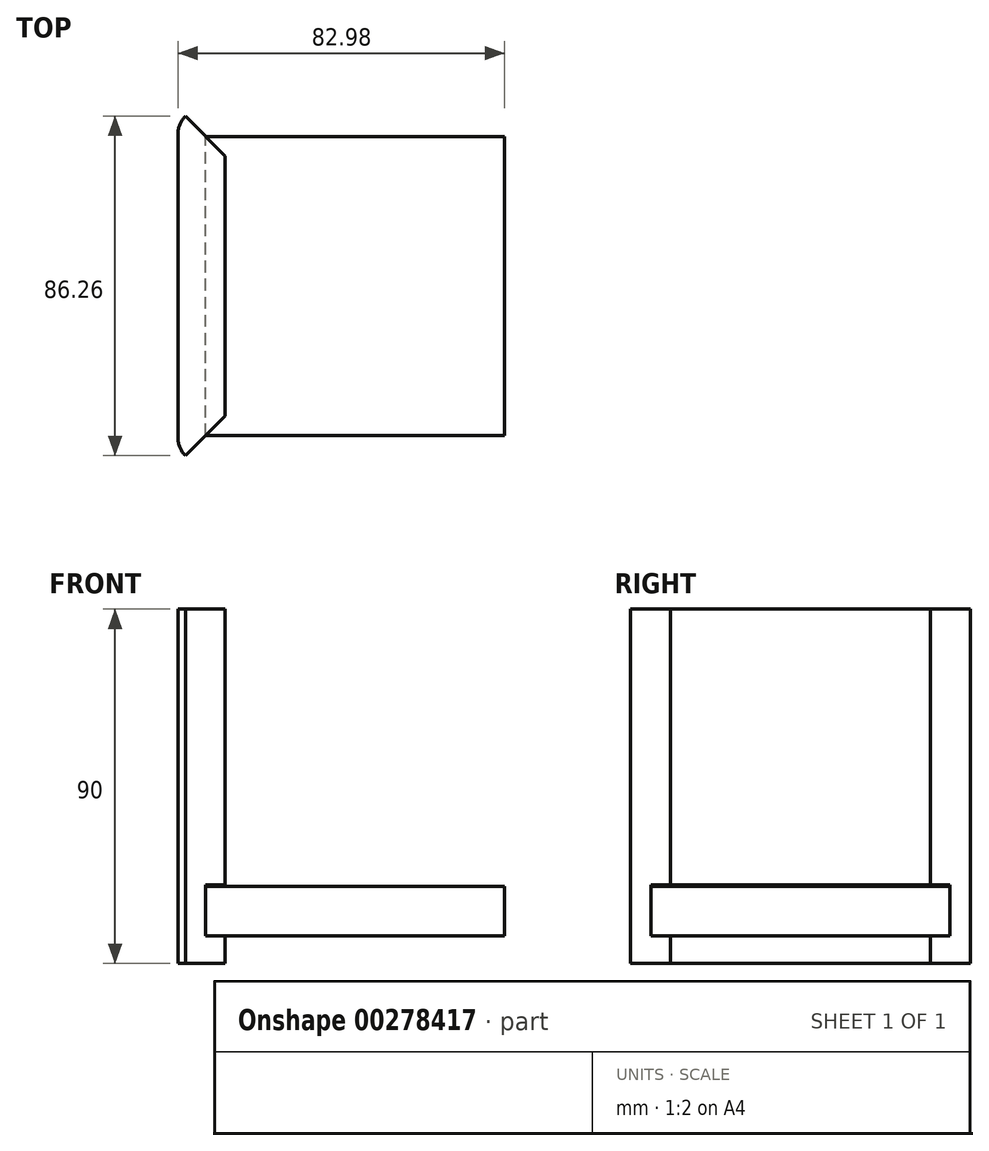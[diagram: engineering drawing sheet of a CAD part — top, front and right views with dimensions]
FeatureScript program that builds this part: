
annotation { "Feature Type Name" : "Feature", "Feature Type Description" : "" }
export const myFeature = defineFeature(function(context is Context, id is Id, definition is map)
    precondition{}
    {
        {
            var Q0;
            Q0=qCreatedBy(makeId("Top.planeOp"),FACE);
            var sketch = newSketch(context, id + "F0", { "sketchPlane" : qUnion([Q0])});
            skLineSegment(sketch, "E0.bottom", {"start": v(38.6, -45) * mm, "end": v(-38.6, -45) * mm});
            skLineSegment(sketch, "E0.top", {"start": v(38.6, 45) * mm, "end": v(-38.6, 45) * mm});
            skLineSegment(sketch, "E0.left", {"start": v(45, -38.6) * mm, "end": v(45, 38.6) * mm});
            skLineSegment(sketch, "E0.right", {"start": v(-45, -38.6) * mm, "end": v(-45, 38.6) * mm});
            skPoint(sketch, "E0.middle", {"position": v(0, 0) * mm});
            skLineSegment(sketch, "E1.0", {"start": v(-33, -33) * mm, "end": v(-33, 33) * mm});
            skLineSegment(sketch, "E1.1", {"start": v(33, -33) * mm, "end": v(-33, -33) * mm});
            skLineSegment(sketch, "E1.2", {"start": v(33, -33) * mm, "end": v(33, 33) * mm});
            skLineSegment(sketch, "E1.3", {"start": v(33, 33) * mm, "end": v(-33, 33) * mm});
            skLineSegment(sketch, "E2", {"start": v(-45, 45) * mm, "end": v(-33, 33) * mm});
            skLineSegment(sketch, "E3", {"start": v(-45, -45) * mm, "end": v(-33, -33) * mm});
            skLineSegment(sketch, "E4", {"start": v(33, 33) * mm, "end": v(45, 45) * mm});
            skLineSegment(sketch, "E5", {"start": v(33, -33) * mm, "end": v(45, -45) * mm});
            skPoint(sketch, "E6.visualSharp", {"position": v(-45, 45) * mm});
            skArc(sketch, "E6.filletArc", {"start": v(-38.6, 45) * mm, "mid": v(-43.13, 43.13) * mm, "end": v(-45, 38.6) * mm});
            skPoint(sketch, "E7.visualSharp", {"position": v(45, 45) * mm});
            skArc(sketch, "E7.filletArc", {"start": v(45, 38.6) * mm, "mid": v(43.13, 43.13) * mm, "end": v(38.6, 45) * mm});
            skPoint(sketch, "E8.visualSharp", {"position": v(45, -45) * mm});
            skArc(sketch, "E8.filletArc", {"start": v(38.6, -45) * mm, "mid": v(43.13, -43.13) * mm, "end": v(45, -38.6) * mm});
            skPoint(sketch, "E9.visualSharp", {"position": v(-45, -45) * mm});
            skArc(sketch, "E9.filletArc", {"start": v(-45, -38.6) * mm, "mid": v(-43.13, -43.13) * mm, "end": v(-38.6, -45) * mm});
            skSolve(sketch);
        }
        {
            var Q0;
            Q0=makeQuery(id+"F0.imprint","IMPRINT",FACE,{"disambiguationData":[TD([[makeQuery(id+"F0.imprint","IMPRINT",EDGE,{"derivedFrom":sQuery(id+"F0.wireOp",EDGE,"E0.right")}),-1.0]])]});
            extrude(context, id + "F1", {"entities" : qUnion([Q0]), "depth" : 90 * mm});
        }
        {
            var Q0;
            Q0=qCreatedBy(makeId("Front.planeOp"),FACE);
            var sketch = newSketch(context, id + "F2", { "sketchPlane" : qUnion([Q0])});
            skLineSegment(sketch, "E10.bottom", {"start": v(-37.98, 20) * mm, "end": v(-32.98, 20) * mm});
            skLineSegment(sketch, "E10.top", {"start": v(-37.98, 7) * mm, "end": v(-32.98, 7) * mm});
            skLineSegment(sketch, "E10.left", {"start": v(-37.98, 20) * mm, "end": v(-37.98, 7) * mm});
            skLineSegment(sketch, "E10.right", {"start": v(-32.98, 20) * mm, "end": v(-32.98, 7) * mm});
            skSolve(sketch);
        }
        {
            var Q0;
            Q0=makeQuery(id+"F2.imprint","IMPRINT",FACE,{"disambiguationData":[TD([[makeQuery(id+"F2.imprint","IMPRINT",EDGE,{"derivedFrom":sQuery(id+"F2.wireOp",EDGE,"E10.bottom")}),-1.0]])]});
            extrude(context, id + "F3", {"entities" : qUnion([Q0]), "operationType" : NewBodyOperationType.REMOVE, "endBound" : BoundingType.SYMMETRIC, "depth" : 89.4 * mm});
        }
        {
            var Q0;
            Q0=makeQuery(id+"F3.boolean.opBoolean","COPY",FACE,{"derivedFrom":makeQuery(id+"F3.opExtrude","SWEPT_FACE",FACE,{"disambiguationData":[OSD([sQuery(id+"F2.wireOp",EDGE,"E10.top")])]})});
            var sketch = newSketch(context, id + "F4", { "sketchPlane" : qUnion([Q0])});
            skLineSegment(sketch, "E11", {"start": v(-37.98, -37.98) * mm, "end": v(-37.98, 37.98) * mm});
            skLineSegment(sketch, "E12", {"start": v(-37.98, 37.98) * mm, "end": v(37.98, 37.98) * mm});
            skLineSegment(sketch, "E13", {"start": v(37.98, 37.98) * mm, "end": v(37.98, -37.98) * mm});
            skLineSegment(sketch, "E14", {"start": v(37.98, -37.98) * mm, "end": v(-37.98, -37.98) * mm});
            skSolve(sketch);
        }
        {
            var Q0;
            Q0=makeQuery(id+"F4.imprint","IMPRINT",FACE,{"disambiguationData":[TD([[makeQuery(id+"F4.imprint","IMPRINT",EDGE,{"derivedFrom":sQuery(id+"F4.wireOp",EDGE,"E11")}),-1.0]])]});
            var Q1;
            Q1=makeQuery(id+"F4.imprint","IMPRINT",FACE,{"disambiguationData":[TD([[makeQuery(id+"F4.imprint","IMPRINT",EDGE,{"derivedFrom":sQuery(id+"F4.wireOp",EDGE,"E12")}),-1.0]])]});
            extrude(context, id + "F5", {"entities" : qUnion([Q0, Q1]), "depth" : 12.5 * mm});
        }
    });
